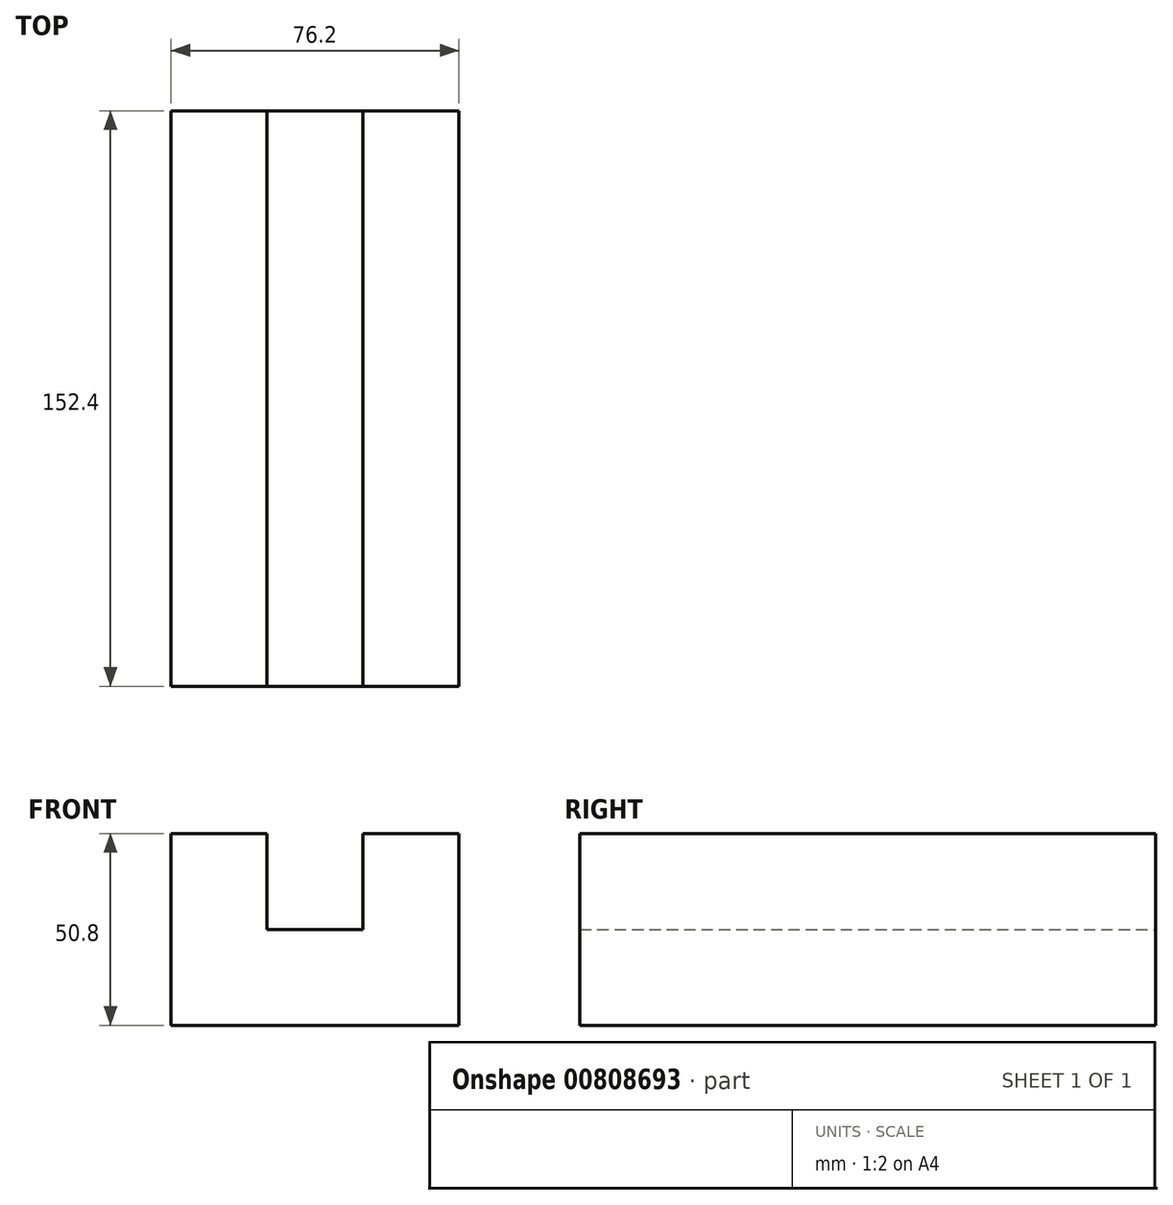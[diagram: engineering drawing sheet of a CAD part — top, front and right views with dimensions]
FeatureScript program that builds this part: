
annotation { "Feature Type Name" : "Feature", "Feature Type Description" : "" }
export const myFeature = defineFeature(function(context is Context, id is Id, definition is map)
    precondition{}
    {
        {
            var Q0;
            Q0=qCreatedBy(makeId("Front.planeOp"),FACE);
            var sketch = newSketch(context, id + "F0", { "sketchPlane" : qUnion([Q0])});
            skLineSegment(sketch, "E0.bottom", {"start": v(-50.8, 0) * mm, "end": v(-25.4, 0) * mm});
            skLineSegment(sketch, "E0.top", {"start": v(-50.8, 50.8) * mm, "end": v(-25.4, 50.8) * mm});
            skLineSegment(sketch, "E0.left", {"start": v(-50.8, 0) * mm, "end": v(-50.8, 50.8) * mm});
            skLineSegment(sketch, "E0.right", {"start": v(-25.4, 0) * mm, "end": v(-25.4, 50.8) * mm});
            skLineSegment(sketch, "E1.bottom", {"start": v(-25.4, 25.4) * mm, "end": v(0, 25.4) * mm});
            skLineSegment(sketch, "E1.top", {"start": v(-25.4, 0) * mm, "end": v(0, 0) * mm});
            skLineSegment(sketch, "E1.left", {"start": v(-25.4, 25.4) * mm, "end": v(-25.4, 0) * mm});
            skLineSegment(sketch, "E1.right", {"start": v(0, 25.4) * mm, "end": v(0, 0) * mm});
            skLineSegment(sketch, "E2.bottom", {"start": v(0, 0) * mm, "end": v(25.4, 0) * mm});
            skLineSegment(sketch, "E2.top", {"start": v(0, 50.8) * mm, "end": v(25.4, 50.8) * mm});
            skLineSegment(sketch, "E2.left", {"start": v(0, 0) * mm, "end": v(0, 50.8) * mm});
            skLineSegment(sketch, "E2.right", {"start": v(25.4, 0) * mm, "end": v(25.4, 50.8) * mm});
            skSolve(sketch);
        }
        {
            var Q0;
            Q0 = qSketchRegion(id + "F0", true);
            extrude(context, id + "F1", {"entities" : qUnion([Q0]), "depth" : 152.4 * mm, "offsetDistance" : 25.4 * mm});
        }
    });
